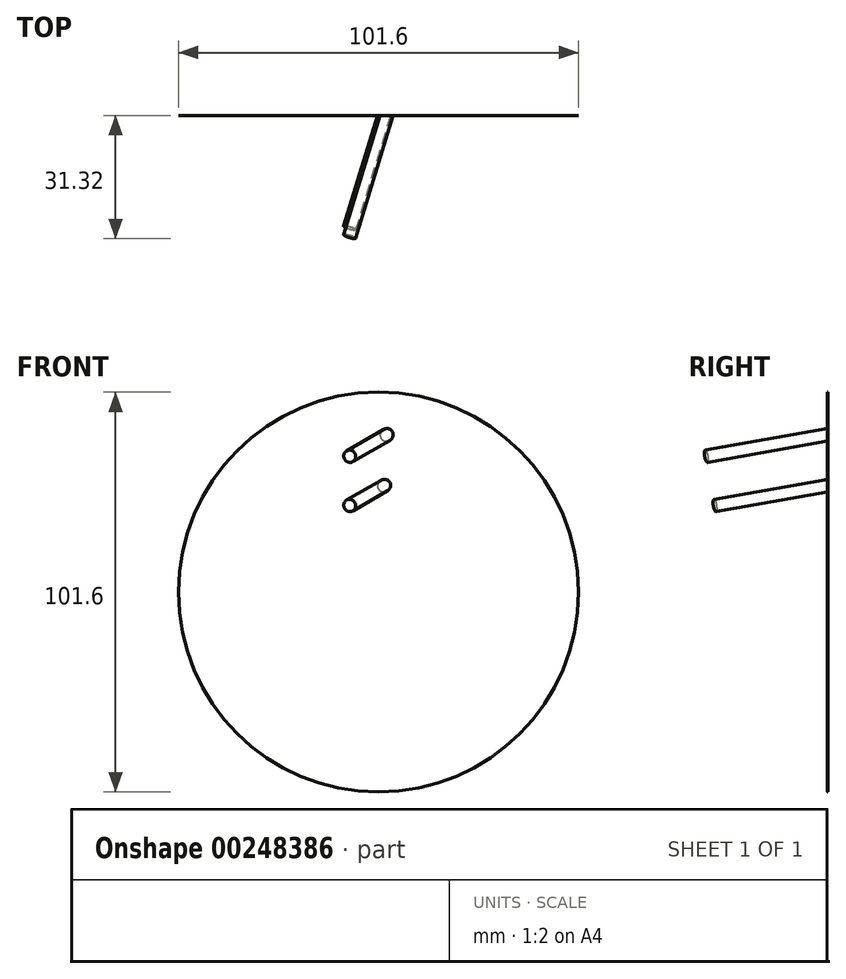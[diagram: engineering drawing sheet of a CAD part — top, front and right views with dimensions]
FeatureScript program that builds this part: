
annotation { "Feature Type Name" : "Feature", "Feature Type Description" : "" }
export const myFeature = defineFeature(function(context is Context, id is Id, definition is map)
    precondition{}
    {
        {
            var Q0;
            Q0=qCreatedBy(makeId("Front.planeOp"),FACE);
            var sketch = newSketch(context, id + "F0", { "sketchPlane" : qUnion([Q0])});
            skCircle(sketch, "E0", {"center": v(0, 0) * mm, "radius": 50.8 * mm});
            skLineSegment(sketch, "E1", {"start": v(0, 0) * mm, "end": v(19.05, 33) * mm, "construction": true});
            skLineSegment(sketch, "E2", {"start": v(0, 0) * mm, "end": v(19.05, -33) * mm, "construction": true});
            skLineSegment(sketch, "E3", {"start": v(0, 0) * mm, "end": v(38.1, 0) * mm, "construction": true});
            skSolve(sketch);
        }
        {
            var Q0;
            Q0=makeQuery(id+"F0.imprint","IMPRINT",FACE,{"disambiguationData":[TD([[makeQuery(id+"F0.imprint","IMPRINT",EDGE,{"derivedFrom":sQuery(id+"F0.wireOp",EDGE,"E0")}),1.0]])]});
            extrude(context, id + "F1", {"entities" : qUnion([Q0]), "oppositeDirection" : true, "depth" : 1 / 101.6 * mm});
        }
        {
            var Q0;
            Q0=qCreatedBy(makeId("Right.planeOp"),FACE);
            var sketch = newSketch(context, id + "F2", { "sketchPlane" : qUnion([Q0])});
            skLineSegment(sketch, "E4.0", {"start": v(0, 0) * mm, "end": v(0, 33) * mm, "construction": true});
            skLineSegment(sketch, "E5", {"start": v(0, 0) * mm, "end": v(-5.73, 32.5) * mm, "construction": true});
            skSolve(sketch);
        }
        {
            var Q0;
            Q0=sQuery(id+"F2.wireOp",VERTEX,"E5.end");
            var Q1;
            Q1=sQuery(id+"F2.wireOp",VERTEX,"E5.start");
            var Q2;
            Q2=sQuery(id+"F0.wireOp",VERTEX,"E2.end");
            cPlane(context, id + "F3", {"entities" : qUnion([Q0, Q1, Q2]), "cplaneType" : CPlaneType.THREE_POINT, "offset" : 25.4 * mm, "width" : 152.4 * mm, "height" : 152.4 * mm});
        }
        {
            var Q0;
            Q0=qCreatedBy(id+"F3.planeOp",FACE);
            cPlane(context, id + "F4", {"entities" : qUnion([Q0]), "cplaneType" : CPlaneType.OFFSET, "offset" : 25.4 * mm, "oppositeDirection" : true, "width" : 152.4 * mm, "height" : 152.4 * mm});
        }
        {
            var Q0;
            Q0=qCreatedBy(id+"F4.planeOp",FACE);
            var sketch = newSketch(context, id + "F5", { "sketchPlane" : qUnion([Q0])});
            skCircle(sketch, "E6", {"center": v(0, 39.35) * mm, "radius": 1.59 * mm});
            skCircle(sketch, "E7", {"center": v(0, 26.65) * mm, "radius": 1.59 * mm});
            skLineSegment(sketch, "E8.0", {"start": v(0, 0) * mm, "end": v(0, 33) * mm, "construction": true});
            skSolve(sketch);
        }
        {
            var Q0;
            Q0=makeQuery(id+"F5.imprint","IMPRINT",FACE,{"disambiguationData":[TD([[makeQuery(id+"F5.imprint","IMPRINT",EDGE,{"derivedFrom":sQuery(id+"F5.wireOp",EDGE,"E7")}),1.0]])]});
            var Q1;
            Q1=makeQuery(id+"F5.imprint","IMPRINT",FACE,{"disambiguationData":[TD([[makeQuery(id+"F5.imprint","IMPRINT",EDGE,{"derivedFrom":sQuery(id+"F5.wireOp",EDGE,"E6")}),1.0]])]});
            extrude(context, id + "F6", {"entities" : qUnion([Q0, Q1]), "endBound" : BoundingType.UP_TO_NEXT, "depth" : 25.4 * mm});
        }
    });
